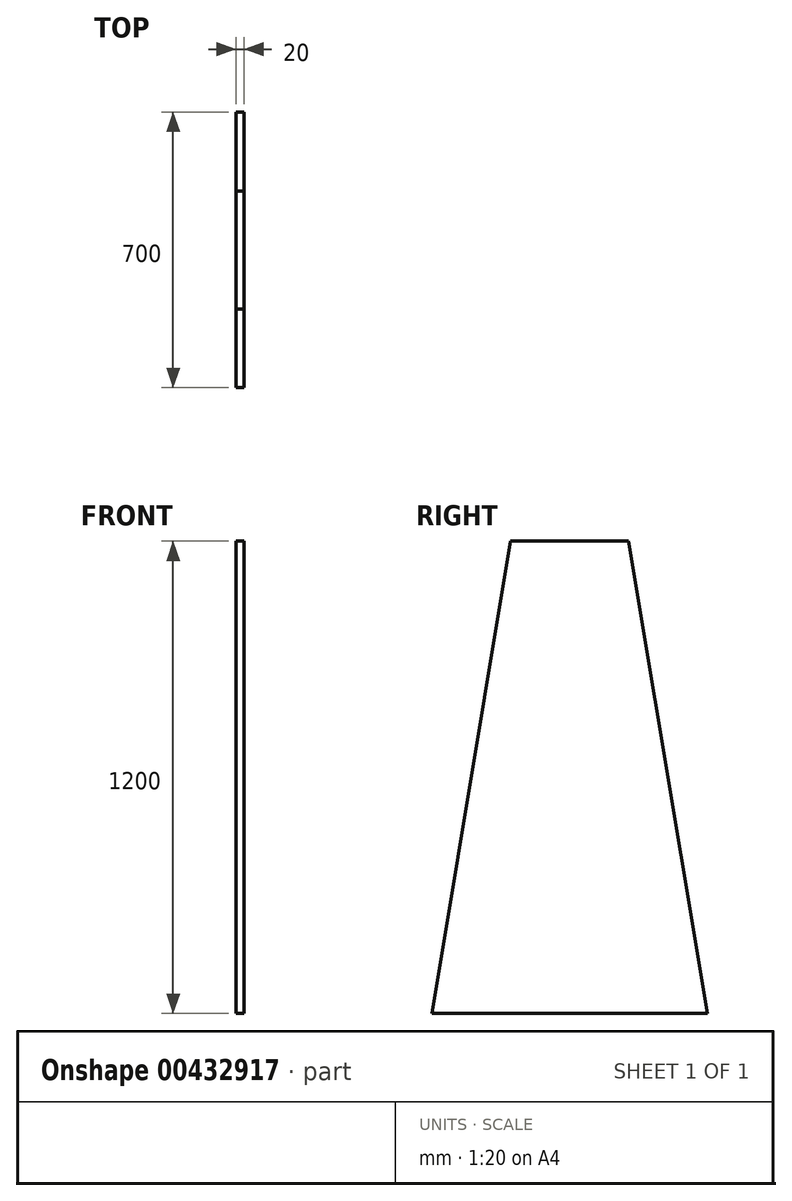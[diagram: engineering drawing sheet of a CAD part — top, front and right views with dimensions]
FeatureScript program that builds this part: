
annotation { "Feature Type Name" : "Feature", "Feature Type Description" : "" }
export const myFeature = defineFeature(function(context is Context, id is Id, definition is map)
    precondition{}
    {
        {
            var Q0;
            Q0=qCreatedBy(makeId("Right.planeOp"),FACE);
            var sketch = newSketch(context, id + "F0", { "sketchPlane" : qUnion([Q0])});
            skLineSegment(sketch, "E0", {"start": v(-150, 500.35) * mm, "end": v(0, 500.35) * mm});
            skLineSegment(sketch, "E1", {"start": v(0, 500.35) * mm, "end": v(0, -699.65) * mm});
            skLineSegment(sketch, "E2", {"start": v(0, -699.65) * mm, "end": v(-350, -699.65) * mm});
            skLineSegment(sketch, "E3", {"start": v(-350, -699.65) * mm, "end": v(-150, 500.35) * mm});
            skLineSegment(sketch, "E4.MirrorCS", {"start": v(150, 500.35) * mm, "end": v(0, 500.35) * mm});
            skLineSegment(sketch, "E5.MirrorCS", {"start": v(350, -699.65) * mm, "end": v(150, 500.35) * mm});
            skLineSegment(sketch, "E6.MirrorCS", {"start": v(0, -699.65) * mm, "end": v(350, -699.65) * mm});
            skSolve(sketch);
        }
        {
            var Q0;
            Q0=makeQuery(id+"F0.imprint","IMPRINT",FACE,{"disambiguationData":[TD([[makeQuery(id+"F0.imprint","IMPRINT",EDGE,{"derivedFrom":sQuery(id+"F0.wireOp",EDGE,"E0")}),-1.0]])]});
            var Q1;
            Q1=makeQuery(id+"F0.imprint","IMPRINT",FACE,{"disambiguationData":[TD([[makeQuery(id+"F0.imprint","IMPRINT",EDGE,{"derivedFrom":sQuery(id+"F0.wireOp",EDGE,"E1")}),1.0]])]});
            extrude(context, id + "F1", {"entities" : qUnion([Q0, Q1]), "depth" : 20 * mm});
        }
    });
